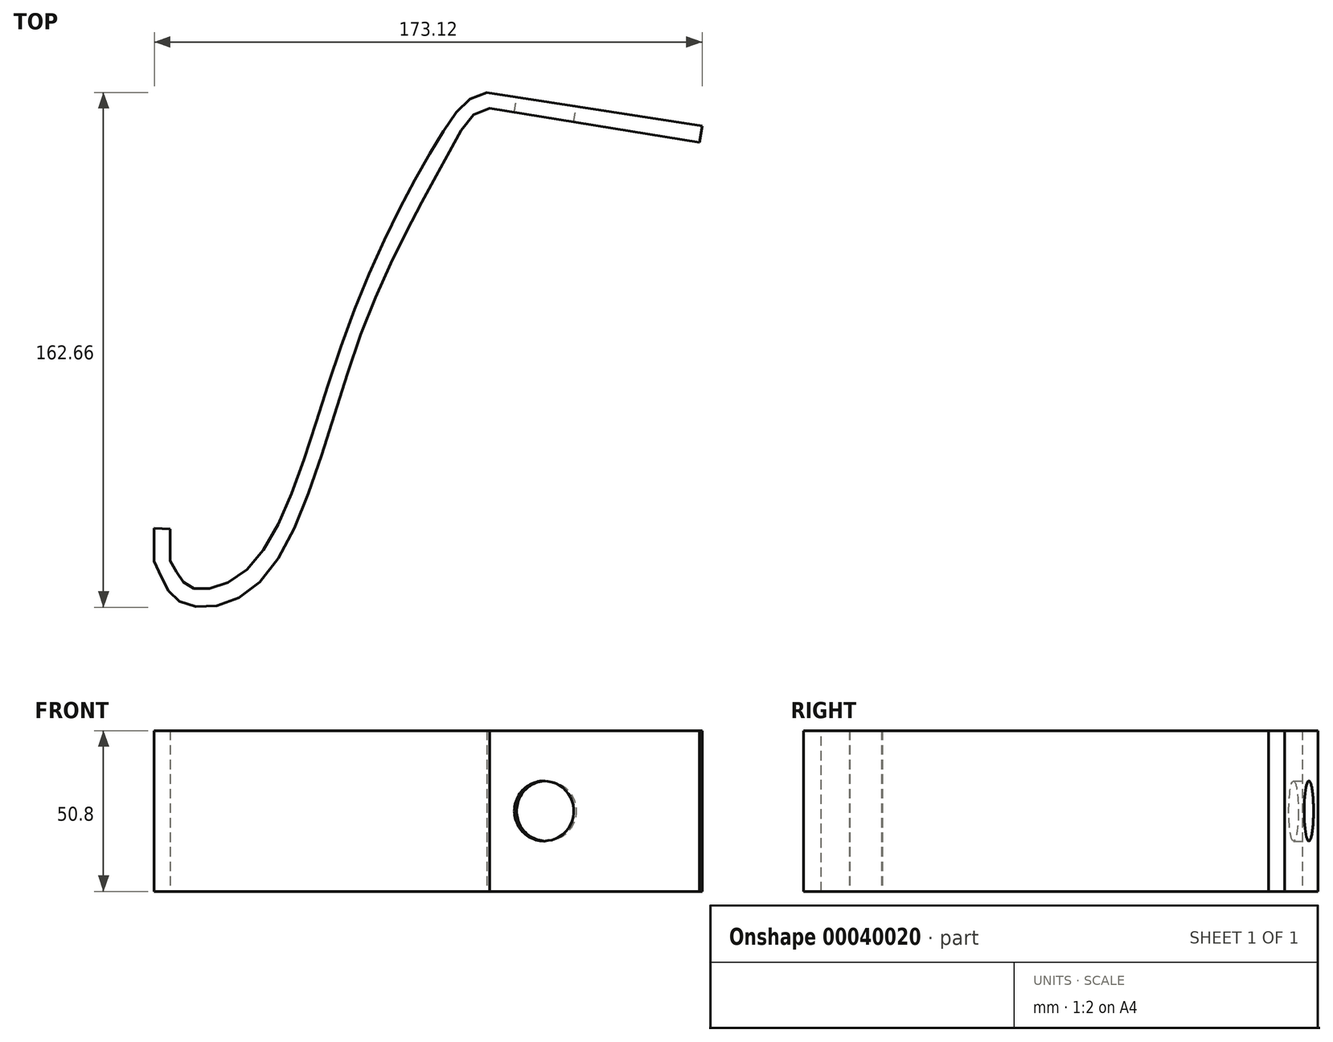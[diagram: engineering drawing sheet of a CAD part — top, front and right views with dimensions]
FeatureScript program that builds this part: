
annotation { "Feature Type Name" : "Feature", "Feature Type Description" : "" }
export const myFeature = defineFeature(function(context is Context, id is Id, definition is map)
    precondition{}
    {
        {
            var Q0;
            Q0=qCreatedBy(makeId("Top.planeOp"),FACE);
            var sketch = newSketch(context, id + "F0", { "sketchPlane" : qUnion([Q0])});
            skFitSpline(sketch, "E0", {"points": [v(-59.6, -69.83) * mm, v(-54.06, -77.79) * mm, v(-35.05, -72.26) * mm, v(-4.96, 0) * mm, v(26.98, 66.4) * mm, v(46.73, 77.68) * mm], "startDerivative": vector(58.05, -78.07) * mm, "endDerivative": vector(190.73, -46.12) * mm});
            skFitSpline(sketch, "E1", {"points": [v(-64.67, -69.93) * mm, v(-56.83, -82.63) * mm, v(-32.62, -77.79) * mm, v(0, 0) * mm, v(29.31, 60.82) * mm, v(45.28, 72.53) * mm], "startDerivative": vector(61.45, -119.14) * mm, "endDerivative": vector(172.87, -57.77) * mm});
            skLineSegment(sketch, "E2", {"start": v(-64.67, -69.93) * mm, "end": v(-64.67, -59.53) * mm});
            skLineSegment(sketch, "E3", {"start": v(-59.6, -69.83) * mm, "end": v(-59.6, -59.74) * mm});
            skLineSegment(sketch, "E4", {"start": v(-59.6, -59.74) * mm, "end": v(-64.67, -59.53) * mm});
            skLineSegment(sketch, "E5", {"start": v(40.43, 78.17) * mm, "end": v(108.45, 67.54) * mm});
            skLineSegment(sketch, "E6", {"start": v(107.63, 62.45) * mm, "end": v(41.27, 73.19) * mm});
            skLineSegment(sketch, "E7", {"start": v(108.45, 67.54) * mm, "end": v(107.63, 62.45) * mm});
            skSolve(sketch);
        }
        {
            var Q0;
            Q0 = qSketchRegion(id + "F0", true);
            extrude(context, id + "F1", {"entities" : qUnion([Q0]), "depth" : 50.8 * mm});
        }
        {
            var Q0;
            Q0=makeQuery(id+"F1.opExtrude","SWEPT_FACE",FACE,{"disambiguationData":[OSD([sQuery(id+"F0.wireOp",EDGE,"E5")])]});
            var sketch = newSketch(context, id + "F2", { "sketchPlane" : qUnion([Q0])});
            skCircle(sketch, "E8", {"center": v(-46.94, 25.4) * mm, "radius": 9.53 * mm});
            skSolve(sketch);
        }
        {
            var Q0;
            Q0=sQuery(id+"F2.wireOp",VERTEX,"E8.center");
            var Q1;
            Q1=makeQuery(id+"F1.opExtrude","SWEPT_BODY",BODY,{"disambiguationData":[OSD([sQuery(id+"F0.wireOp",EDGE,"E0"),sQuery(id+"F0.wireOp",EDGE,"E1"),sQuery(id+"F0.wireOp",EDGE,"E2"),sQuery(id+"F0.wireOp",EDGE,"E3"),sQuery(id+"F0.wireOp",EDGE,"E4"),sQuery(id+"F0.wireOp",EDGE,"E5"),sQuery(id+"F0.wireOp",EDGE,"E6"),sQuery(id+"F0.wireOp",EDGE,"E7")])]});
            hole(context, id + "F3", {"style" : HoleStyle.SIMPLE, "holeDiameter" : 19.05 * mm, "endStyle" : HoleEndStyle.THROUGH, "locations" : qUnion([Q0]), "scope" : qUnion([Q1])});
        }
    });
